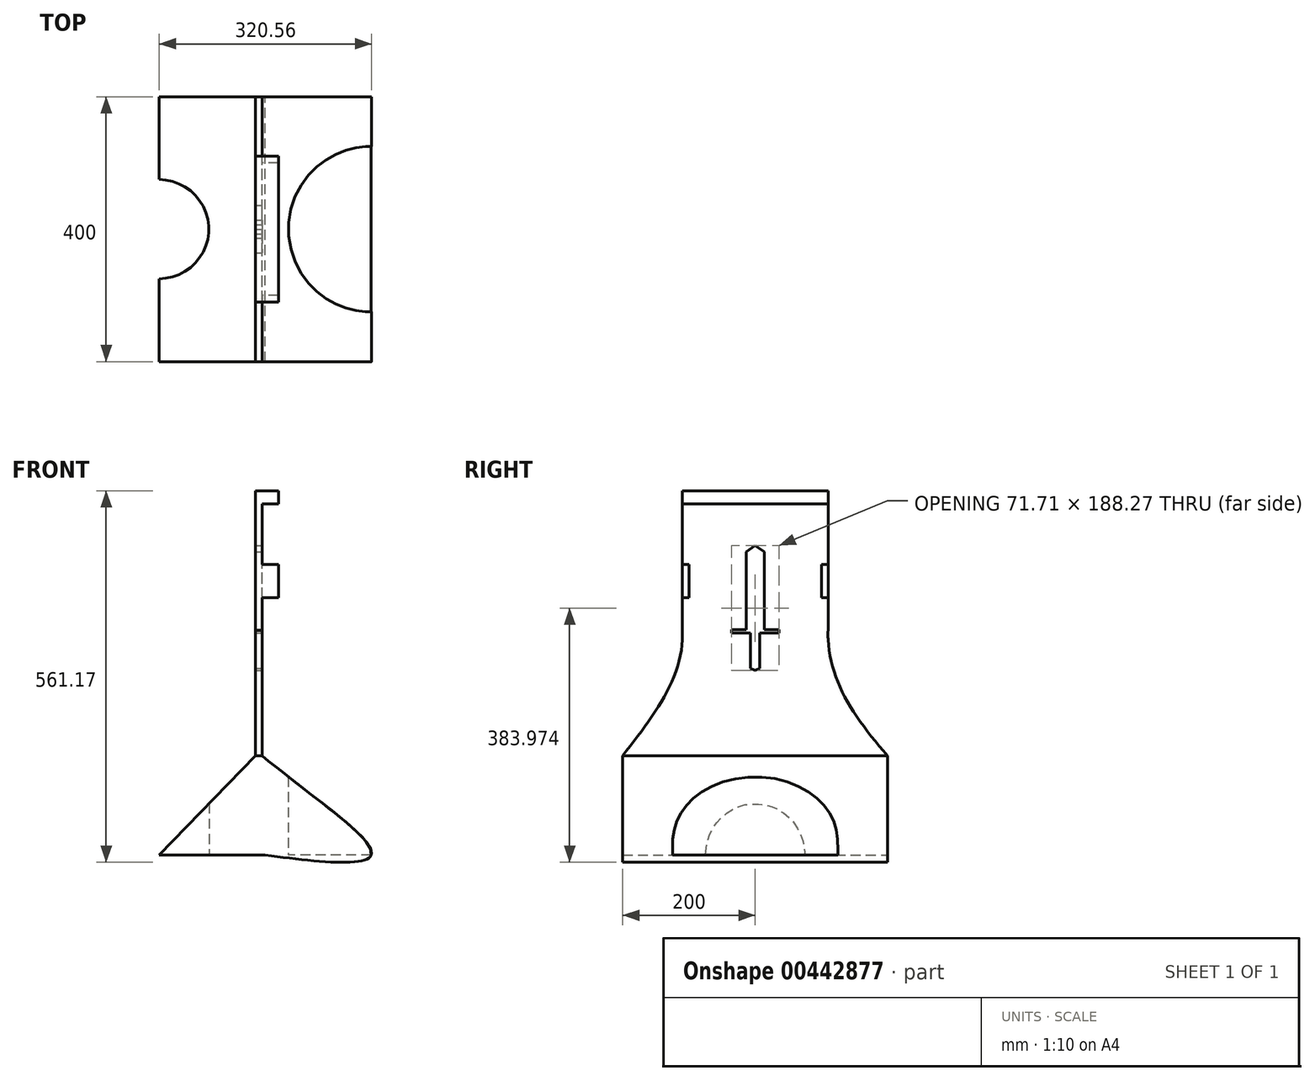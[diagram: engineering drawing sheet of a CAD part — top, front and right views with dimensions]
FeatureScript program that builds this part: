
annotation { "Feature Type Name" : "Feature", "Feature Type Description" : "" }
export const myFeature = defineFeature(function(context is Context, id is Id, definition is map)
    precondition{}
    {
        {
            var Q0;
            Q0=qCreatedBy(makeId("Front.planeOp"),FACE);
            var sketch = newSketch(context, id + "F0", { "sketchPlane" : qUnion([Q0])});
            skFitSpline(sketch, "E0", {"points": [v(0, 0) * mm, v(160, 0) * mm, v(-5, 150) * mm], "startDerivative": vector(446.66, -62.32) * mm, "endDerivative": vector(-420, 349.65) * mm});
            skLineSegment(sketch, "E1", {"start": v(0, 0) * mm, "end": v(160, 0) * mm});
            skLineSegment(sketch, "E2", {"start": v(-5, 150) * mm, "end": v(-15, 150) * mm});
            skLineSegment(sketch, "E3", {"start": v(-10, 0) * mm, "end": v(0, 0) * mm});
            skLineSegment(sketch, "E4", {"start": v(-10, 0) * mm, "end": v(-60, 0) * mm});
            skLineSegment(sketch, "E5", {"start": v(-60, 0) * mm, "end": v(-160, 0) * mm});
            skLineSegment(sketch, "E6", {"start": v(-160, 0) * mm, "end": v(-15, 150) * mm});
            skSolve(sketch);
        }
        {
            var Q0;
            Q0 = qSketchRegion(id + "F0", true);
            extrude(context, id + "F1", {"entities" : qUnion([Q0]), "depth" : 400 * mm});
        }
        {
            var Q0;
            Q0=makeQuery(id+"F1.opExtrude","SWEPT_FACE",FACE,{"disambiguationData":[OSD([sQuery(id+"F0.wireOp",EDGE,"E1"),sQuery(id+"F0.wireOp",EDGE,"E3"),sQuery(id+"F0.wireOp",EDGE,"E4"),sQuery(id+"F0.wireOp",EDGE,"E5")])]});
            var sketch = newSketch(context, id + "F2", { "sketchPlane" : qUnion([Q0])});
            skCircle(sketch, "E7", {"center": v(-160, 200) * mm, "radius": 75 * mm});
            skCircle(sketch, "E8", {"center": v(160, 200) * mm, "radius": 125 * mm});
            skSolve(sketch);
        }
        {
            var Q0;
            Q0 = qSketchRegion(id + "F2", true);
            extrude(context, id + "F3", {"entities" : qUnion([Q0]), "operationType" : NewBodyOperationType.REMOVE, "oppositeDirection" : true, "depth" : 160 * mm});
        }
        {
            var Q0;
            Q0=makeQuery(id+"F1.opExtrude","SWEPT_FACE",FACE,{"disambiguationData":[OSD([sQuery(id+"F0.wireOp",EDGE,"E2")])]});
            var sketch = newSketch(context, id + "F4", { "sketchPlane" : qUnion([Q0])});
            skLineSegment(sketch, "E9", {"start": v(-15, 0) * mm, "end": v(-5, 0) * mm});
            skLineSegment(sketch, "E10", {"start": v(-5, 0) * mm, "end": v(-5, -400) * mm});
            skLineSegment(sketch, "E11", {"start": v(-5, -400) * mm, "end": v(-15, -400) * mm});
            skLineSegment(sketch, "E12", {"start": v(-15, -400) * mm, "end": v(-15, 0) * mm});
            skSolve(sketch);
        }
        {
            var Q0;
            Q0 = qSketchRegion(id + "F4", true);
            extrude(context, id + "F5", {"entities" : qUnion([Q0]), "operationType" : NewBodyOperationType.ADD, "depth" : 400 * mm});
        }
        {
            var Q0;
            Q0=makeQuery(id+"F5.opExtrude","SWEPT_FACE",FACE,{"disambiguationData":[OSD([sQuery(id+"F4.wireOp",EDGE,"E10")])]});
            var sketch = newSketch(context, id + "F6", { "sketchPlane" : qUnion([Q0])});
            skFitSpline(sketch, "E13", {"points": [v(-400, 150) * mm, v(-310, 325.03) * mm, v(-400, 550) * mm], "startDerivative": vector(276.28, 355.34) * mm, "endDerivative": vector(-266.89, 443.14) * mm});
            skLineSegment(sketch, "E14", {"start": v(-400, 550) * mm, "end": v(-400, 150) * mm});
            skLineSegment(sketch, "E15", {"start": v(-400, 550) * mm, "end": v(0, 550) * mm});
            skFitSpline(sketch, "E16", {"points": [v(0, 550) * mm, v(-90, 325.03) * mm, v(0, 150) * mm], "startDerivative": vector(-305.13, -444.7) * mm, "endDerivative": vector(315.32, -353.8) * mm});
            skLineSegment(sketch, "E17", {"start": v(-400, 150) * mm, "end": v(-400, 550) * mm});
            skLineSegment(sketch, "E18", {"start": v(-300, 550) * mm, "end": v(-100, 550) * mm});
            skLineSegment(sketch, "E19", {"start": v(-100, 550) * mm, "end": v(0, 550) * mm});
            skLineSegment(sketch, "E20", {"start": v(0, 150) * mm, "end": v(0, 550) * mm});
            skLineSegment(sketch, "E21", {"start": v(0, 550) * mm, "end": v(-100, 550) * mm});
            skPoint(sketch, "E22.end.orphan", {"position": v(-354.98, 472.3) * mm});
            skLineSegment(sketch, "E23", {"start": v(-355.02, 472.38) * mm, "end": v(-355.02, 472.38) * mm});
            skPoint(sketch, "E24.start.orphan", {"position": v(-48.03, 472.03) * mm});
            skLineSegment(sketch, "E25", {"start": v(-310, 325.03) * mm, "end": v(-310, 550) * mm});
            skLineSegment(sketch, "E26", {"start": v(-90, 325.03) * mm, "end": v(-90, 550) * mm});
            skPoint(sketch, "E27.centerSnap0", {"position": v(-200, 550) * mm});
            skLineSegment(sketch, "E28", {"start": v(-310, 550) * mm, "end": v(-90, 550) * mm});
            skLineSegment(sketch, "E29", {"start": v(-90, 530) * mm, "end": v(-90, 550) * mm});
            skLineSegment(sketch, "E30", {"start": v(-310, 550) * mm, "end": v(-310, 530) * mm});
            skPoint(sketch, "E27.center.orphan", {"position": v(-200, 372.8) * mm});
            skPoint(sketch, "E31.0.midPoint", {"position": v(-200, 298.36) * mm});
            skPoint(sketch, "E32.orphan", {"position": v(-175.81, 298.36) * mm});
            skPoint(sketch, "E31.1.start.orphan", {"position": v(-224.19, 298.36) * mm});
            skPoint(sketch, "E33.end.orphan", {"position": v(-200, 278.67) * mm});
            skPoint(sketch, "E33.start.orphan", {"position": v(-200, 466.94) * mm});
            skPoint(sketch, "E34.end.orphan", {"position": v(-114.14, 372.8) * mm});
            skPoint(sketch, "E34.start.orphan", {"position": v(-285.86, 372.8) * mm});
            skPoint(sketch, "E35.end.orphan", {"position": v(-114.14, 432.8) * mm});
            skPoint(sketch, "E35.start.orphan", {"position": v(-174.14, 372.8) * mm});
            skPoint(sketch, "E36.end.orphan", {"position": v(-285.86, 432.8) * mm});
            skPoint(sketch, "E36.start.orphan", {"position": v(-225.86, 372.8) * mm});
            skPoint(sketch, "E37.start.orphan", {"position": v(-242.93, 449.87) * mm});
            skPoint(sketch, "E38.start.orphan", {"position": v(-157.07, 449.87) * mm});
            skPoint(sketch, "E39.0.start.orphan", {"position": v(-169.17, 298.36) * mm});
            skPoint(sketch, "E39.1.start.orphan", {"position": v(-230.83, 298.36) * mm});
            skPoint(sketch, "E40.start.orphan", {"position": v(-200, 205.9) * mm});
            skPoint(sketch, "E41.start.orphan", {"position": v(-200, 340.28) * mm});
            skLineSegment(sketch, "E42", {"start": v(-186.14, 457.8) * mm, "end": v(-200, 466.94) * mm});
            skLineSegment(sketch, "E43", {"start": v(-213.86, 457.8) * mm, "end": v(-200, 466.94) * mm});
            skLineSegment(sketch, "E44", {"start": v(-225.86, 340.28) * mm, "end": v(-235.86, 340.28) * mm});
            skLineSegment(sketch, "E45", {"start": v(-174.14, 340.28) * mm, "end": v(-164.14, 340.28) * mm});
            skLineSegment(sketch, "E46", {"start": v(-164.14, 340.28) * mm, "end": v(-164.14, 335.28) * mm});
            skLineSegment(sketch, "E47", {"start": v(-235.86, 340.28) * mm, "end": v(-235.86, 335.28) * mm});
            skLineSegment(sketch, "E48", {"start": v(-164.14, 335.28) * mm, "end": v(-186.14, 335.28) * mm});
            skLineSegment(sketch, "E49", {"start": v(-193.07, 281.97) * mm, "end": v(-200, 278.67) * mm});
            skPoint(sketch, "E50.end.orphan", {"position": v(-202.15, 278.67) * mm});
            skLineSegment(sketch, "E51", {"start": v(-200, 278.67) * mm, "end": v(-206.93, 281.97) * mm});
            skLineSegment(sketch, "E52.trimOffspring", {"start": v(-213.86, 335.28) * mm, "end": v(-235.86, 335.28) * mm});
            skLineSegment(sketch, "E53", {"start": v(-193.07, 281.97) * mm, "end": v(-193.07, 335.28) * mm});
            skLineSegment(sketch, "E54", {"start": v(-206.93, 281.97) * mm, "end": v(-206.93, 335.28) * mm});
            skLineSegment(sketch, "E55", {"start": v(-206.93, 335.28) * mm, "end": v(-213.86, 335.28) * mm});
            skLineSegment(sketch, "E56", {"start": v(-193.07, 335.28) * mm, "end": v(-186.14, 335.28) * mm});
            skPoint(sketch, "E57.orphan", {"position": v(-186.14, 285.28) * mm});
            skPoint(sketch, "E58.end.orphan", {"position": v(-213.86, 285.28) * mm});
            skLineSegment(sketch, "E59", {"start": v(-174.14, 340.28) * mm, "end": v(-186.14, 340.28) * mm});
            skLineSegment(sketch, "E60", {"start": v(-186.14, 340.28) * mm, "end": v(-186.14, 457.8) * mm});
            skLineSegment(sketch, "E61", {"start": v(-213.86, 340.28) * mm, "end": v(-213.86, 458.4) * mm});
            skPoint(sketch, "E61.endSnap0", {"position": v(-212.93, 458.4) * mm});
            skPoint(sketch, "E62.end.orphan", {"position": v(-174.14, 449.87) * mm});
            skPoint(sketch, "E63.orphan", {"position": v(-225.86, 449.87) * mm});
            skLineSegment(sketch, "E64", {"start": v(-225.86, 340.28) * mm, "end": v(-213.86, 340.28) * mm});
            skSolve(sketch);
        }
        {
            var Q0;
            Q0 = qSketchRegion(id + "F6", true);
            extrude(context, id + "F7", {"entities" : qUnion([Q0]), "operationType" : NewBodyOperationType.REMOVE, "oppositeDirection" : true, "depth" : 369 * mm});
        }
        {
            var Q0;
            Q0 = qSketchRegion(id + "F6", true);
            extrude(context, id + "F8", {"entities" : qUnion([Q0]), "operationType" : NewBodyOperationType.REMOVE, "oppositeDirection" : true, "depth" : 744 * mm});
        }
        {
            var Q0;
            Q0 = qSketchRegion(id + "F6", true);
            extrude(context, id + "F9", {"entities" : qUnion([Q0]), "operationType" : NewBodyOperationType.REMOVE, "oppositeDirection" : true, "depth" : 294 * mm});
        }
        {
            var Q0;
            Q0 = qSketchRegion(id + "F6", true);
            extrude(context, id + "F10", {"entities" : qUnion([Q0]), "operationType" : NewBodyOperationType.REMOVE, "oppositeDirection" : true, "depth" : 25 * mm});
        }
        {
            var Q0;
            Q0=makeQuery(id+"F5.opExtrude","SWEPT_FACE",FACE,{"disambiguationData":[OSD([sQuery(id+"F4.wireOp",EDGE,"E10")])]});
            var sketch = newSketch(context, id + "F11", { "sketchPlane" : qUnion([Q0])});
            skLineSegment(sketch, "E65", {"start": v(-310, 550) * mm, "end": v(-310, 530) * mm});
            skLineSegment(sketch, "E66", {"start": v(-310, 530) * mm, "end": v(-90, 530) * mm});
            skLineSegment(sketch, "E67", {"start": v(-90, 530) * mm, "end": v(-90, 550) * mm});
            skLineSegment(sketch, "E68", {"start": v(-90, 550) * mm, "end": v(-310, 550) * mm});
            skSolve(sketch);
        }
        {
            var Q0;
            Q0 = qSketchRegion(id + "F11", true);
            extrude(context, id + "F12", {"entities" : qUnion([Q0]), "operationType" : NewBodyOperationType.ADD, "depth" : 25 * mm});
        }
        {
            var Q0;
            Q0=makeQuery(id+"F5.opExtrude","SWEPT_FACE",FACE,{"disambiguationData":[OSD([sQuery(id+"F4.wireOp",EDGE,"E10")])]});
            var sketch = newSketch(context, id + "F13", { "sketchPlane" : qUnion([Q0])});
            skLineSegment(sketch, "E69", {"start": v(-310, 388.57) * mm, "end": v(-300, 388.57) * mm});
            skLineSegment(sketch, "E70", {"start": v(-300, 388.57) * mm, "end": v(-300, 438.57) * mm});
            skLineSegment(sketch, "E71", {"start": v(-300, 438.57) * mm, "end": v(-310, 438.57) * mm});
            skLineSegment(sketch, "E72", {"start": v(-310, 438.57) * mm, "end": v(-310, 388.57) * mm});
            skLineSegment(sketch, "E73", {"start": v(-310, 388.57) * mm, "end": v(-310, 438.57) * mm});
            skLineSegment(sketch, "E74", {"start": v(-90, 438.57) * mm, "end": v(-100, 438.57) * mm});
            skLineSegment(sketch, "E75", {"start": v(-100, 438.57) * mm, "end": v(-100, 388.57) * mm});
            skLineSegment(sketch, "E76", {"start": v(-100, 388.57) * mm, "end": v(-90, 388.57) * mm});
            skLineSegment(sketch, "E77", {"start": v(-90, 438.57) * mm, "end": v(-90, 388.57) * mm});
            skSolve(sketch);
        }
        {
            var Q0;
            Q0 = qSketchRegion(id + "F13", true);
            extrude(context, id + "F14", {"entities" : qUnion([Q0]), "operationType" : NewBodyOperationType.ADD, "depth" : 25 * mm});
        }
    });
